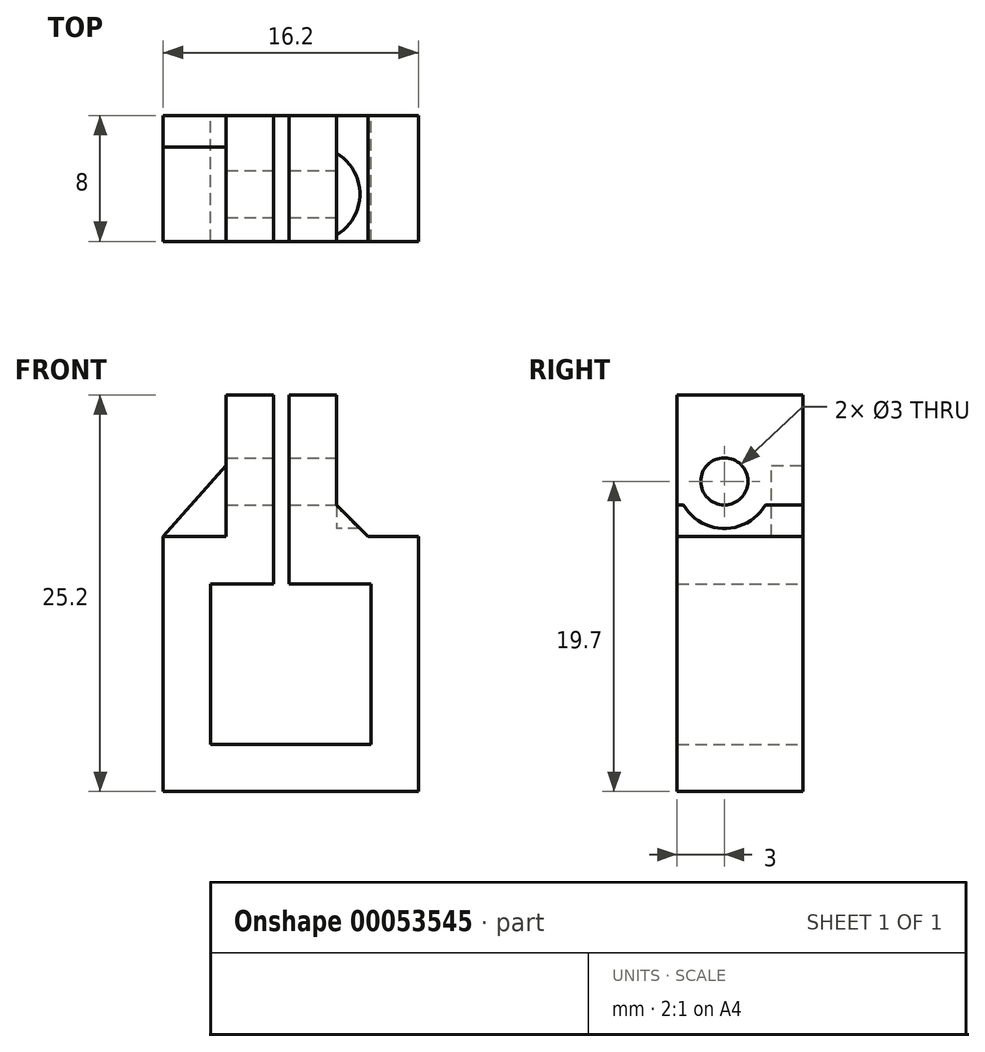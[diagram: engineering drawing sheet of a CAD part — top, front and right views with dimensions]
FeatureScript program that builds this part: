
annotation { "Feature Type Name" : "Feature", "Feature Type Description" : "" }
export const myFeature = defineFeature(function(context is Context, id is Id, definition is map)
    precondition{}
    {
        {
            var Q0;
            Q0=qCreatedBy(makeId("Front.planeOp"),FACE);
            var sketch = newSketch(context, id + "F0", { "sketchPlane" : qUnion([Q0])});
            skLineSegment(sketch, "E0.rect.bottom", {"start": v(5.1, -5.1) * mm, "end": v(-5.1, -5.1) * mm});
            skLineSegment(sketch, "E0.rect.top", {"start": v(5.1, 5.1) * mm, "end": v(-0.1, 5.1) * mm});
            skLineSegment(sketch, "E0.rect.left", {"start": v(5.1, -5.1) * mm, "end": v(5.1, 5.1) * mm});
            skLineSegment(sketch, "E0.rect.right", {"start": v(-5.1, -5.1) * mm, "end": v(-5.1, 5.1) * mm});
            skPoint(sketch, "E0.rect.middle", {"position": v(0, 0) * mm});
            skLineSegment(sketch, "E1.0", {"start": v(8.1, 8.1) * mm, "end": v(2.9, 8.1) * mm});
            skLineSegment(sketch, "E1.1", {"start": v(8.1, -8.1) * mm, "end": v(8.1, 8.1) * mm});
            skLineSegment(sketch, "E1.2", {"start": v(8.1, -8.1) * mm, "end": v(-8.1, -8.1) * mm});
            skLineSegment(sketch, "E1.3", {"start": v(-8.1, -8.1) * mm, "end": v(-8.1, 8.1) * mm});
            skLineSegment(sketch, "E2", {"start": v(-4.1, 8.1) * mm, "end": v(-4.1, 17.1) * mm});
            skLineSegment(sketch, "E3", {"start": v(-4.1, 17.1) * mm, "end": v(-1.1, 17.1) * mm});
            skLineSegment(sketch, "E4", {"start": v(-1.1, 17.1) * mm, "end": v(-1.1, 8.1) * mm});
            skLineSegment(sketch, "E5", {"start": v(-0.1, 17.1) * mm, "end": v(-0.1, 8.1) * mm});
            skLineSegment(sketch, "E6", {"start": v(-0.1, 17.1) * mm, "end": v(2.9, 17.1) * mm});
            skLineSegment(sketch, "E7", {"start": v(2.9, 17.1) * mm, "end": v(2.9, 8.1) * mm});
            skLineSegment(sketch, "E8", {"start": v(-4.1, 8.1) * mm, "end": v(-5.1, 8.1) * mm});
            skLineSegment(sketch, "E9", {"start": v(-8.1, 8.1) * mm, "end": v(-4.1, 8.1) * mm});
            skPoint(sketch, "E10.end.orphan", {"position": v(-5.1, 17.1) * mm});
            skLineSegment(sketch, "E11", {"start": v(-4.1, 5.1) * mm, "end": v(-5.1, 5.1) * mm});
            skLineSegment(sketch, "E12", {"start": v(-1.1, 8.1) * mm, "end": v(-1.1, 5.1) * mm});
            skLineSegment(sketch, "E13", {"start": v(-0.1, 8.1) * mm, "end": v(-0.1, 5.1) * mm});
            skPoint(sketch, "E13.endSnap0", {"position": v(0.5, 5.1) * mm});
            skLineSegment(sketch, "E14.trimOffspring", {"start": v(-1.1, 5.1) * mm, "end": v(-4.1, 5.1) * mm});
            skSolve(sketch);
        }
        {
            var Q0;
            Q0=qSketchRegion(id+"F0",true);
            extrude(context, id + "F1", {"entities" : qUnion([Q0]), "depth" : 8 * mm});
        }
        {
            var Q0;
            Q0=makeQuery(id+"F1.opExtrude","SWEPT_FACE",FACE,{"disambiguationData":[OSD([sQuery(id+"F0.wireOp",EDGE,"E4")])]});
            var sketch = newSketch(context, id + "F2", { "sketchPlane" : qUnion([Q0])});
            skCircle(sketch, "E15", {"center": v(-5, 11.6) * mm, "radius": 1.5 * mm});
            skPoint(sketch, "E15.centerSnap0", {"position": v(-9, 11.6) * mm});
            skPoint(sketch, "E15.centerSnap1", {"position": v(-5, 16.1) * mm});
            skSolve(sketch);
        }
        {
            var Q0;
            Q0=qSketchRegion(id+"F2",true);
            extrude(context, id + "F3", {"entities" : qUnion([Q0]), "operationType" : NewBodyOperationType.REMOVE, "oppositeDirection" : true, "depth" : 25 * mm, "symmetric" : true});
        }
        {
            var Q0;
            Q0=makeQuery(id+"F1.opExtrude","SWEPT_EDGE",EDGE,{"disambiguationData":[OSD([sQuery(id+"F0.wireOp",EDGE,"E1.0"),sQuery(id+"F0.wireOp",EDGE,"E7")])]});
            chamfer(context, id + "F4", {"entities" : qUnion([Q0]), "width" : 2 * mm, "tangentPropagation" : true});
        }
        {
            var Q0;
            Q0=makeQuery(id+"F1.opExtrude","SWEPT_FACE",FACE,{"disambiguationData":[OSD([sQuery(id+"F0.wireOp",EDGE,"E7")])]});
            var sketch = newSketch(context, id + "F5", { "sketchPlane" : qUnion([Q0])});
            skCircle(sketch, "E16", {"center": v(-5, 11.6) * mm, "radius": 3 * mm});
            skSolve(sketch);
        }
        {
            var Q0;
            Q0 = qSketchRegion(id + "F5", true);
            extrude(context, id + "F6", {"entities" : qUnion([Q0]), "operationType" : NewBodyOperationType.REMOVE, "depth" : 4 * mm});
        }
        {
            var Q0;
            Q0=makeQuery(id+"F1.opExtrude","CAP_FACE",FACE,{"disambiguationData":[OSD([sQuery(id+"F0.wireOp",EDGE,"E0.rect.bottom"),sQuery(id+"F0.wireOp",EDGE,"E0.rect.top"),sQuery(id+"F0.wireOp",EDGE,"E0.rect.left"),sQuery(id+"F0.wireOp",EDGE,"E0.rect.right"),sQuery(id+"F0.wireOp",EDGE,"E1.0"),sQuery(id+"F0.wireOp",EDGE,"E1.1"),sQuery(id+"F0.wireOp",EDGE,"E1.2"),sQuery(id+"F0.wireOp",EDGE,"E1.3"),sQuery(id+"F0.wireOp",EDGE,"E2"),sQuery(id+"F0.wireOp",EDGE,"E3"),sQuery(id+"F0.wireOp",EDGE,"E4"),sQuery(id+"F0.wireOp",EDGE,"E5"),sQuery(id+"F0.wireOp",EDGE,"E6"),sQuery(id+"F0.wireOp",EDGE,"E7"),sQuery(id+"F0.wireOp",EDGE,"E9"),sQuery(id+"F0.wireOp",EDGE,"E11"),sQuery(id+"F0.wireOp",EDGE,"E12"),sQuery(id+"F0.wireOp",EDGE,"E13"),sQuery(id+"F0.wireOp",EDGE,"E14.trimOffspring")])],"isStart":true});
            var sketch = newSketch(context, id + "F7", { "sketchPlane" : qUnion([Q0])});
            skLineSegment(sketch, "E17", {"start": v(8.1, 8.1) * mm, "end": v(4.1, 12.6) * mm});
            skLineSegment(sketch, "E18", {"start": v(4.1, 12.6) * mm, "end": v(4.1, 8.1) * mm});
            skLineSegment(sketch, "E19", {"start": v(4.1, 8.1) * mm, "end": v(8.1, 8.1) * mm});
            skSolve(sketch);
        }
        {
            var Q0;
            Q0 = qSketchRegion(id + "F7", true);
            extrude(context, id + "F8", {"entities" : qUnion([Q0]), "oppositeDirection" : true, "depth" : 2 * mm});
        }
    });
